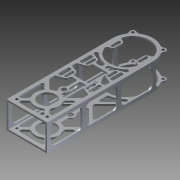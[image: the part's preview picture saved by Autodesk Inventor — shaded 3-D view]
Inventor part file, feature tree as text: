
AUTODESK INVENTOR PART (.ipt)
format: ipt  version: 2012 (Build 160160000, 160)  size: 835,584 bytes
history: native  units: in
note: dims shown in document units (in); Inventor stores cm internally (conversion verified against a paired STEP export)
features: extrude x7, sketch x5, thread x4, fillet x3
ambient origin geometry x8: Origin, YZ Plane, XZ Plane, XY Plane, X Axis, Y Axis, Z Axis, Center Point
bodies: Solid1 (feature_tree)
feature tree (19):
  extrude  "Extrusion1"  Depth=3.0in
  sketch  "Sketch2"  dims[d2=0.125in d3=0.125in d4=0.125in]
  extrude  "Extrusion2"  Depth=0.125in
  fillet  "Fillet1"  Radius=0.125in
  sketch  "Sketch3"  dims[d5=0.125in d6=10.0in d7=0.0in]
  extrude  "Extrusion3"  Depth=10.0in TaperAngle=0.0deg
  extrude  "Extrusion4"  Depth=1.5in
  fillet  "Fillet2"  Radius=1.5in
  extrude  "Extrusion5"  Depth=1.5in
  fillet  "Fillet3"  Radius=0.5in
  extrude  "Extrusion6"  Depth=0.366in
  extrude  "Extrusion7"  Depth=1.75in
  thread  "Thread1"  [1 undecoded]
  thread  "Thread2"  [1 undecoded]
  thread  "Thread3"  [1 undecoded]
  thread  "Thread4"  [1 undecoded]
  sketch  "Sketch1"  dims[d0=2.0in d1=3.0in]
  sketch  "Sketch4"  dims[d8=1.25in d9=1.5in d10=1.5in]
  sketch  "Sketch5"  dims[d11=1.3125in d15=1.5in d18=0.5in d30=0.366in d31=1.75in d32=0.125in d33=0.125in d34=0.125in d35=0.125in d36=0.125in d37=0.125in d38=0.25in d39=0.25in d41=0.25in d42=0.875in d43=1.5in d44=0.125in d45=0.125in d46=0.125in d47=0.125in d48=0.3125in d49=0.25in d50=0.0in d51=0.125in d52=0.5in d53=0.1in d54=0.5in d55=0.1in d56=0.5in d57=0.1in d58=0.5in d59=0.1in d60=1.6in d61=1.6in d62=0.5in d63=0.5in d64=0.8in d65=0.8in d66=3.0in d70=0.1in d71=2.0in d74=2.0in d75=2.5in d76=0.2in d77=0.2in d78=1.5in d79=0.25in d80=0.25in d81=0.25in d82=0.25in d83=0.1in d84=1.0in d85=0.0in d86=0.5in d87=0.5in d89=1.0in d90=7.375in d91=2.5in d92=0.366in d94=0.125in d95=0.125in d96=0.875in d97=0.25in d98=0.25in d99=0.25in d100=0.125in d101=0.125in d102=0.25in d103=0.2in d106=0.1875in d107=0.0938in d108=0.1875in d109=0.0938in d110=0.0938in d111=0.1875in d112=0.3in d113=0.125in d114=0.481in d115=0.481in d116=0.2in d119=1.4375in d120=0.1875in d121=0.0938in d123=1.2in d124=0.481in d125=0.481in d126=0.125in d127=0.0in d128=0.125in d129=0.25in d133=0.125in d172=0.125in d173=0.0in d174=0.25in d175=0.25in d176=0.25in d177=0.25in d178=0.25in d179=3.0in d181=0.125in d183=0.125in d184=2.625in d185=1.1811in d187=2.625in d188=0.3937in d190=1.0in d192=0.125in d193=0.125in d194=0.125in d195=0.125in d196=0.125in d197=0.125in d198=0.125in d199=0.125in d200=0.481in d201=1.25in d202=4.75in d203=45.0deg d204=0.0938in d205=0.1875in d206=0.1875in d209=0.0625in d210=0.0in d211=0.375in d212=0.201in d213=9.0in d214=0.375in d216=0.25in d218=0.375in d221=0.25in d222=0.625in d223=0.125in d224=0.125in d226=0.25in d227=0.0625in d228=0.0in d229=1.0in d230=0.0in d231=1.0in d232=0.0in d233=1.0in d234=0.0in d235=1.0in d236=0.0in d237=7.375in d238=0.2in]
note: 4 required parameter values undecoded (feature->parameter linkage not recoverable at this tier; creation-order binding heuristic only, values carry confidence <= 0.55)
